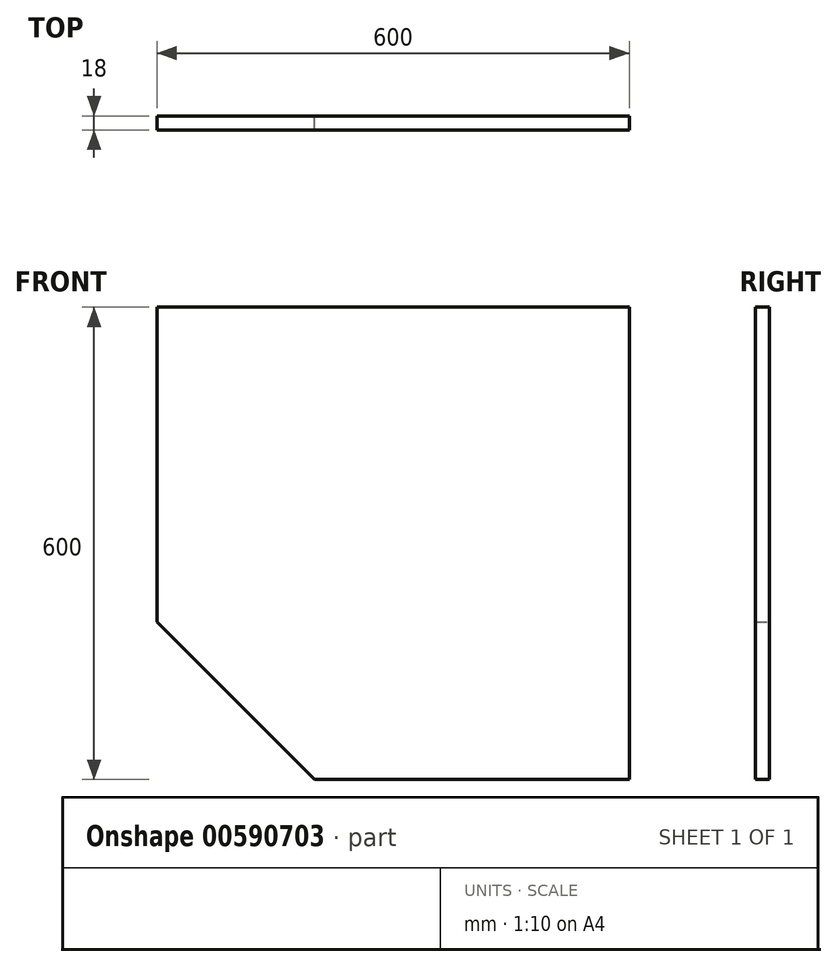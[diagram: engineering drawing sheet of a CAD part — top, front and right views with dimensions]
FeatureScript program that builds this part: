
annotation { "Feature Type Name" : "Feature", "Feature Type Description" : "" }
export const myFeature = defineFeature(function(context is Context, id is Id, definition is map)
    precondition{}
    {
        {
            var Q0;
            Q0=qCreatedBy(makeId("Front.planeOp"),FACE);
            var sketch = newSketch(context, id + "F0", { "sketchPlane" : qUnion([Q0])});
            skLineSegment(sketch, "E0.bottom", {"start": v(300, -300) * mm, "end": v(-100, -300) * mm});
            skLineSegment(sketch, "E0.top", {"start": v(300, 300) * mm, "end": v(-300, 300) * mm});
            skLineSegment(sketch, "E0.left", {"start": v(300, -300) * mm, "end": v(300, 300) * mm});
            skLineSegment(sketch, "E0.right", {"start": v(-300, -100) * mm, "end": v(-300, 300) * mm});
            skPoint(sketch, "E0.middle", {"position": v(0, 0) * mm});
            skLineSegment(sketch, "E1", {"start": v(-300, -100) * mm, "end": v(-100, -300) * mm});
            skPoint(sketch, "E2.orphan", {"position": v(-300, -300) * mm});
            skSolve(sketch);
        }
        {
            var Q0;
            Q0=makeQuery(id+"F0.imprint","IMPRINT",FACE,{"disambiguationData":[TD([[makeQuery(id+"F0.imprint","IMPRINT",EDGE,{"derivedFrom":sQuery(id+"F0.wireOp",EDGE,"E0.bottom")}),-1.0]])]});
            extrude(context, id + "F1", {"entities" : qUnion([Q0]), "depth" : 18 * mm, "offsetDistance" : 25 * mm});
        }
    });
